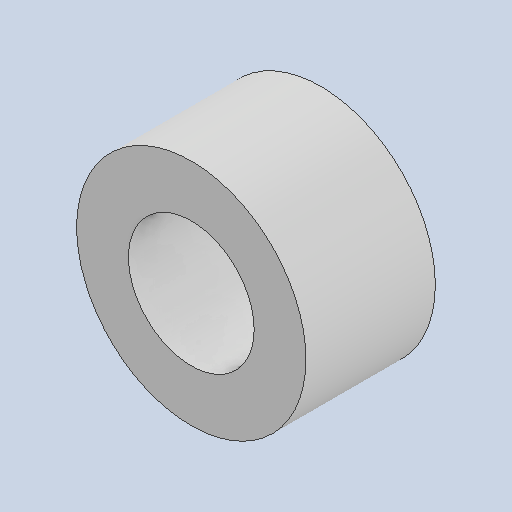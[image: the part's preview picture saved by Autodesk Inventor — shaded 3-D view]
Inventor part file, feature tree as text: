
AUTODESK INVENTOR PART (.ipt)
format: ipt  version: 2024 (Build 280153000, 153)  size: 100,352 bytes
history: native  units: in
note: dims shown in document units (in); Inventor stores cm internally (conversion verified against a paired STEP export)
features: extrude x1, sketch x1
ambient origin geometry x8: Origin, YZ Plane, XZ Plane, XY Plane, X Axis, Y Axis, Z Axis, Center Point
bodies: Solid1 (feature_tree)
feature tree (2):
  extrude  "Extrusion1"  Depth=0.175in
  sketch  "Sketch1"  dims[d0=0.17in d1=0.07in d2=0.175in d3=0.0in]
